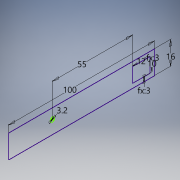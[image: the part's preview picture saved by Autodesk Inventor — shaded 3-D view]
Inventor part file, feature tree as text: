
AUTODESK INVENTOR PART (.ipt)
format: ipt  version: 2018 (Build 220112000, 112)  size: 95,232 bytes
history: native  units: mm
features: sketch x1
ambient origin geometry x8: Origin, YZ Plane, XZ Plane, XY Plane, X Axis, Y Axis, Z Axis, Center Point
feature tree (1):
  sketch  "Sketch1"  dims[d0=12.0mm d1=10.0mm d2=3.2mm d3=55.0mm d4=16.0mm d5=3.0mm d6=100.0mm d7=3.0mm]
